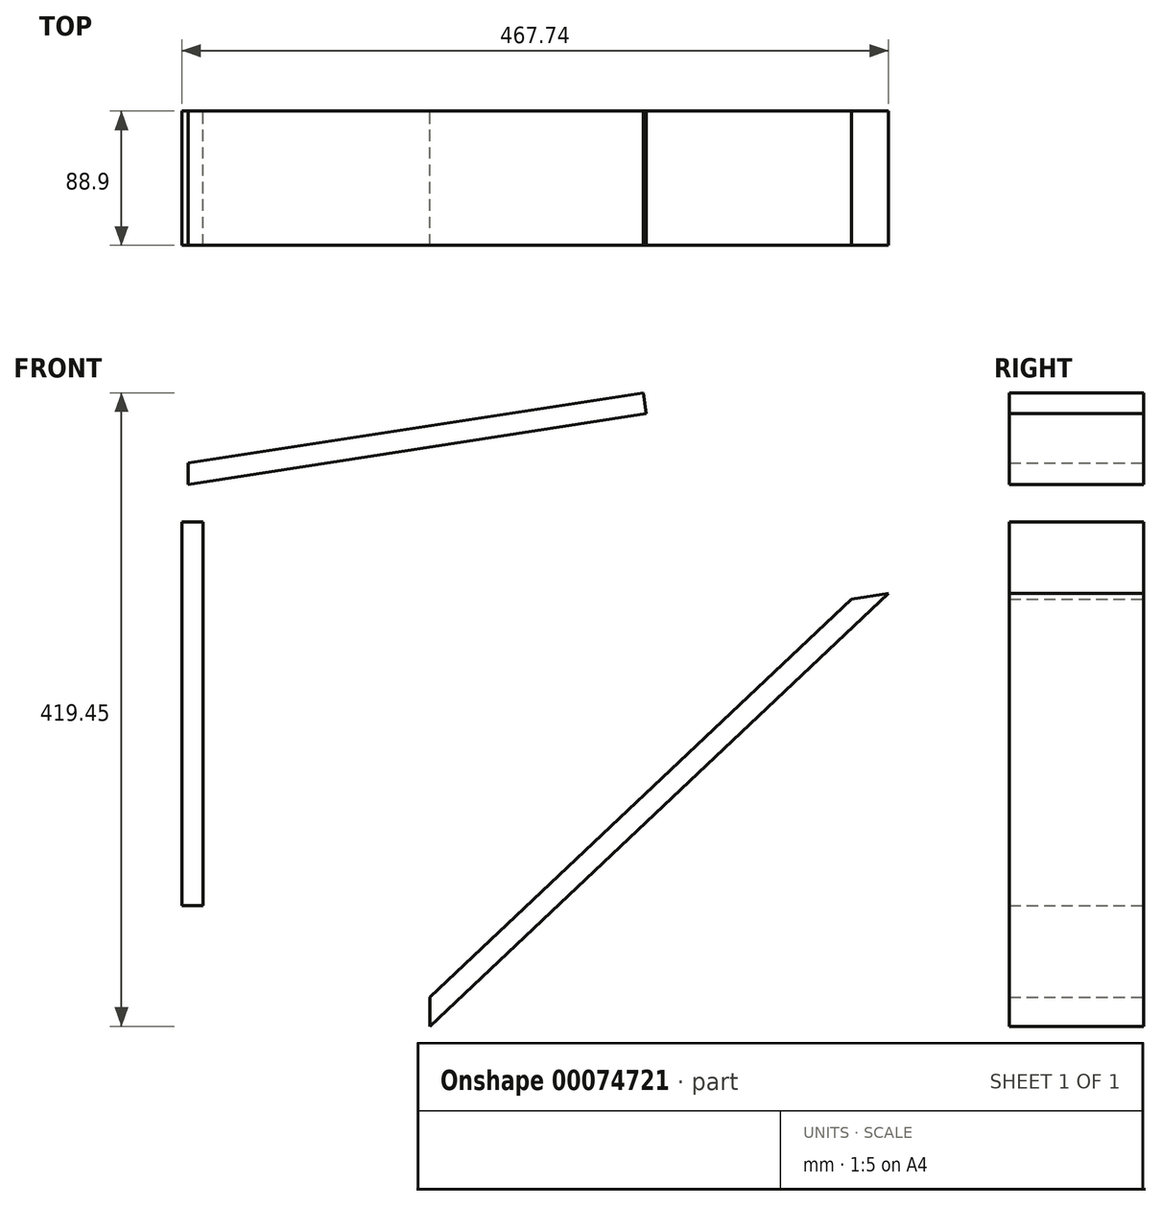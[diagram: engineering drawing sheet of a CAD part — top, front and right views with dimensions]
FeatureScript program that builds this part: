
annotation { "Feature Type Name" : "Feature", "Feature Type Description" : "" }
export const myFeature = defineFeature(function(context is Context, id is Id, definition is map)
    precondition{}
    {
        {
            var Q0;
            Q0=qCreatedBy(makeId("Front.planeOp"),FACE);
            var sketch = newSketch(context, id + "F0", { "sketchPlane" : qUnion([Q0])});
            skLineSegment(sketch, "E0", {"start": v(348.89, 183.11) * mm, "end": v(45.36, -103.43) * mm});
            skLineSegment(sketch, "E1.0", {"start": v(324.51, 179.35) * mm, "end": v(45.36, -84.18) * mm});
            skLineSegment(sketch, "E2", {"start": v(324.51, 179.35) * mm, "end": v(348.89, 183.11) * mm});
            skLineSegment(sketch, "E3", {"start": v(45.36, -84.18) * mm, "end": v(45.36, -103.43) * mm});
            skSolve(sketch);
        }
        {
            var Q0;
            Q0=qCreatedBy(makeId("Front.planeOp"),FACE);
            var sketch = newSketch(context, id + "F1", { "sketchPlane" : qUnion([Q0])});
            skLineSegment(sketch, "E4.left", {"start": v(-104.85, -23.49) * mm, "end": v(-104.85, 230.51) * mm});
            skLineSegment(sketch, "E4.right", {"start": v(-118.85, -23.49) * mm, "end": v(-118.85, 230.51) * mm});
            skLineSegment(sketch, "E5", {"start": v(-104.85, -23.49) * mm, "end": v(-118.85, -23.49) * mm});
            skLineSegment(sketch, "E6", {"start": v(-104.85, 230.51) * mm, "end": v(-118.85, 230.51) * mm});
            skSolve(sketch);
        }
        {
            var Q0;
            Q0=qCreatedBy(makeId("Front.planeOp"),FACE);
            var sketch = newSketch(context, id + "F2", { "sketchPlane" : qUnion([Q0])});
            skLineSegment(sketch, "E7", {"start": v(-114.73, 269.47) * mm, "end": v(186.5, 316.02) * mm});
            skLineSegment(sketch, "E8.0", {"start": v(-114.73, 255.3) * mm, "end": v(188.63, 302.19) * mm});
            skLineSegment(sketch, "E9", {"start": v(188.63, 302.19) * mm, "end": v(186.5, 316.02) * mm});
            skLineSegment(sketch, "E10", {"start": v(-114.73, 255.3) * mm, "end": v(-114.73, 269.47) * mm});
            skSolve(sketch);
        }
        {
            var Q0;
            Q0=makeQuery(id+"F2.imprint","IMPRINT",FACE,{"disambiguationData":[TD([[makeQuery(id+"F2.imprint","IMPRINT",EDGE,{"derivedFrom":sQuery(id+"F2.wireOp",EDGE,"E7")}),-1.0]])]});
            extrude(context, id + "F3", {"entities" : qUnion([Q0]), "depth" : 88.9 * mm});
        }
        {
            var Q0;
            Q0=makeQuery(id+"F1.imprint","IMPRINT",FACE,{"disambiguationData":[TD([[makeQuery(id+"F1.imprint","IMPRINT",EDGE,{"derivedFrom":sQuery(id+"F1.wireOp",EDGE,"E4.left")}),1.0]])]});
            extrude(context, id + "F4", {"entities" : qUnion([Q0]), "depth" : 88.9 * mm});
        }
        {
            var Q0;
            Q0=makeQuery(id+"F0.imprint","IMPRINT",FACE,{"disambiguationData":[TD([[makeQuery(id+"F0.imprint","IMPRINT",EDGE,{"derivedFrom":sQuery(id+"F0.wireOp",EDGE,"E0")}),-1.0]])]});
            extrude(context, id + "F5", {"entities" : qUnion([Q0]), "depth" : 88.9 * mm});
        }
    });
